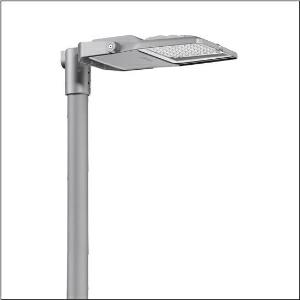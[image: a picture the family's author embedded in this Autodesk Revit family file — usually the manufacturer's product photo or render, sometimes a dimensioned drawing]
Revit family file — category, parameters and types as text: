
# Revit family: floodlight_fl_21_mini___pl64_5xa7775b2e3a_7162
name_source: partatom
category: Lighting Fixtures
units: mm (PartAtom-declared; Revit-internal decimal feet)

## family parameters
Cut with Voids When Loaded = No
Host = Face
Light Source = No
Part Type = Normal
Room Calculation Point = No
Round Connector Dimension = Use Diameter
Shared = No

## types (1)
- --- (1 x LED, 6010 lm, 45.7 W, 3000K)
    Apparent Load = 46 VA
    CIE Flux Codes = 28 80 98 100 100
    Color Rendering = 70
    Color Temperature = 3000K
    Default Elevation = 1800 mm
    Description = Floodlight FL 21 mini, floodlight, primary light control with lens, of PMMA, primary optical cover: protective disc, of toughened safety glass, transparent, light distribution: PL64, light emission: direct distribution, installation type: surface-mounted, LED, High Power LED, rated luminous flux: 6.010lm, luminous efficacy: 132lm/W, light colour: 730, colour temperature: 3000K, control gear: Smart Interface (Zhaga), control: flexible luminous flux parameterisation, time-dependent luminous flux control, constant luminous flux control, overheat protection, pre-setting: logarithmic dimming characteristic, with terminal, 6-pole, mains connection: 220..240V, AC, 50/60Hz, start of lifetime: 46W, end of service life: 48W, reduction: 22W, luminaire housing, of diecast aluminium, powder-coated, SITECO metallic grey (DB 702S), corrosivity category C5 mid according to DIN EN ISO 12944, suitable for swimming pools, chlorine-resistant, sealing non-destructively replaceable, please order mast flange separately, mast bracket, of steel, galvanised, powder-coated, SITECO metallic grey (DB 702S), Smart Interface above, protection rating (complete): IP66, insulation class (complete): insulation class II (safety insulation), certification: CE, ENEC, VDE, protection symbol: D, impact resistance: IK08, permissible operating ambient temperature: -40..+40°C, permissible operating ambient temperature for outdoor applications: -40..+50°C, standard: DIN EN 12944, LABS conformity tested according to VDMA 24364:2018-05, packaging unit: 1 piece

Light Distribution: PL64
    Height = 70 mm
    Lamp = 1 x LED
    Lamp Light Flux = 6010 lm
    Lamp Power = 45.7 W
    Lamp count = 1
    Length = 485 mm
    Luminous efficacy = 132 lm/W
    Manufacturer = Siteco
    ModVariant = No
    Model = 5XA7775B2E3A
    Mounting Place = Pole
    Mounting Type = Pole annexe
    Number of Poles = 1
    OnlyDefault = Yes
    Power Factor = 1
    Product Name = Floodlight FL 21 mini | PL64
    Product group = floodlight | pylon annexe
    ProductGroupID = 6201
    Protection Class = Protection class II
    Protection Degree = IP 66
    RLX_Detail_Level = 1
    RLX_Emergency_Light_Flux = 0 lm
    RLX_Emergency_Type = 0
    RLX_Emergency_Type_DB = No
    RlxData = <blob elided: 101181 chars, md5=98046519>
    Socket = socket
    Standby Power = 0 W
    System Light Flux = 6010 lm
    System Power = 46 W
    Type Comments = factory setting: luminous flux: 100 % | dim-lin: 254 | 463 mA
    Type Image = l_1007125.jpg
    URL = http://relux.com
    VarID = @adj_166577
    Voltage = 0 V
    Weight = 0.00 kg
    Width = 337 mm

## geometry (parser evidence)
native form markers: Blend x4, Sweep x13
no freeform markers — native parametric forms only
